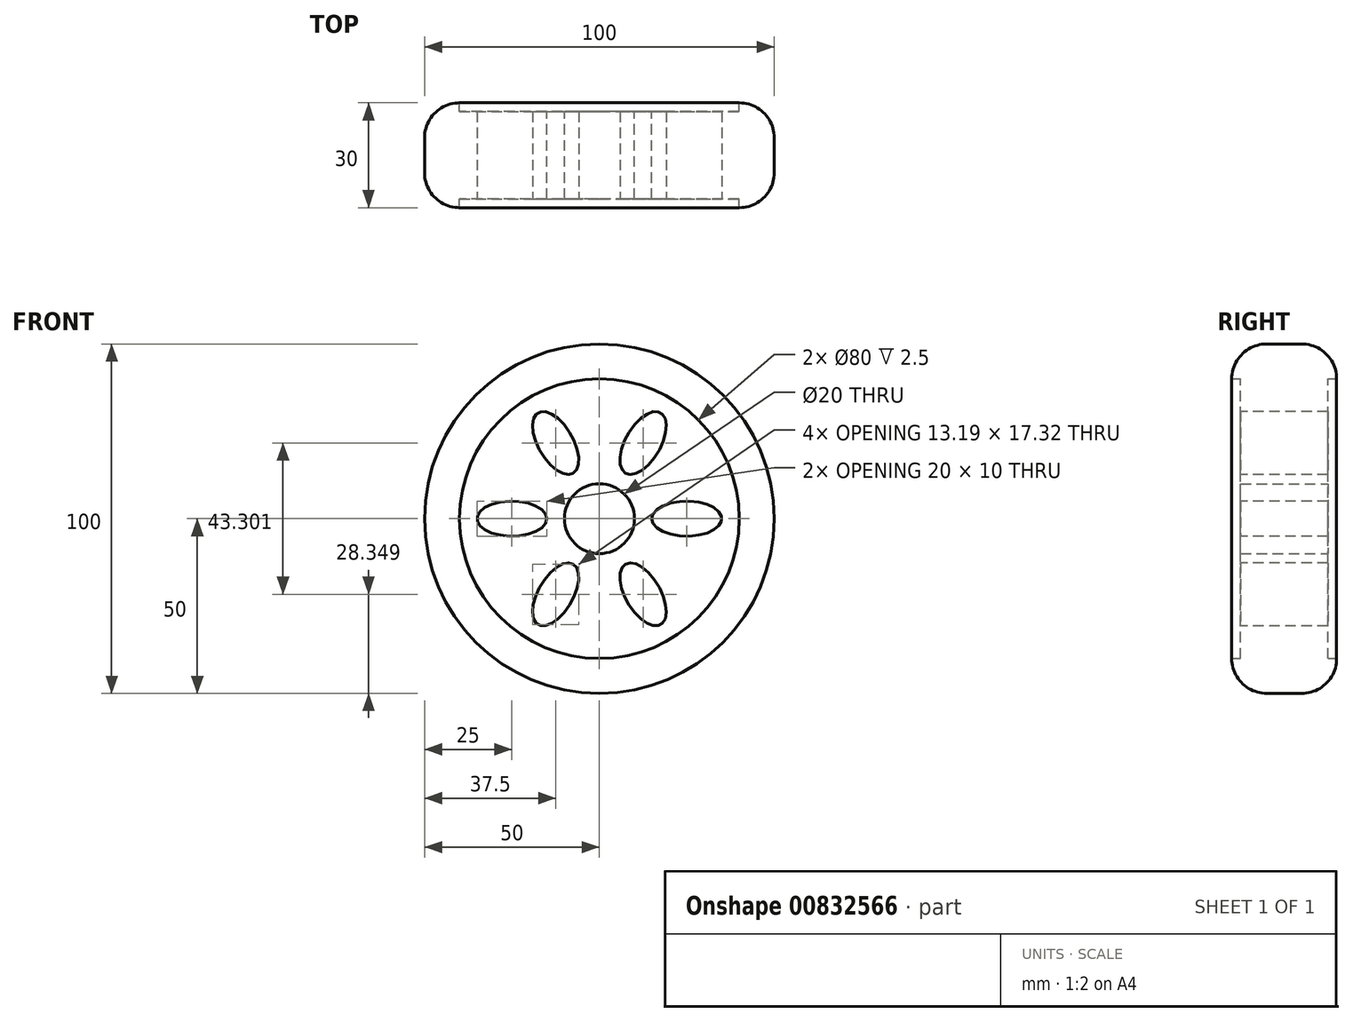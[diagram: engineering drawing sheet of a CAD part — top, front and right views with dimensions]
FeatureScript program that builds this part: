
annotation { "Feature Type Name" : "Feature", "Feature Type Description" : "" }
export const myFeature = defineFeature(function(context is Context, id is Id, definition is map)
    precondition{}
    {
        {
            var Q0;
            Q0=qCreatedBy(makeId("Front.planeOp"),FACE);
            var sketch = newSketch(context, id + "F0", { "sketchPlane" : qUnion([Q0])});
            skCircle(sketch, "E0", {"center": v(0, 0) * mm, "radius": 50 * mm});
            skCircle(sketch, "E1", {"center": v(0, 0) * mm, "radius": 40 * mm});
            skSolve(sketch);
        }
        {
            var Q0;
            Q0=makeQuery(id+"F0.imprint","IMPRINT",FACE,{"disambiguationData":[TD([[makeQuery(id+"F0.imprint","IMPRINT",EDGE,{"derivedFrom":sQuery(id+"F0.wireOp",EDGE,"E0")}),1.0]])]});
            extrude(context, id + "F1", {"entities" : qUnion([Q0]), "endBound" : BoundingType.SYMMETRIC, "depth" : 30 * mm, "offsetDistance" : 25 * mm});
        }
        {
            var Q0;
            Q0=makeQuery(id+"F0.imprint","IMPRINT",FACE,{"disambiguationData":[TD([[makeQuery(id+"F0.imprint","IMPRINT",EDGE,{"derivedFrom":sQuery(id+"F0.wireOp",EDGE,"E1")}),1.0]])]});
            extrude(context, id + "F2", {"entities" : qUnion([Q0]), "operationType" : NewBodyOperationType.ADD, "endBound" : BoundingType.SYMMETRIC, "depth" : 25 * mm, "offsetDistance" : 25 * mm});
        }
        {
            var Q0;
            Q0=makeQuery(id+"F2.opExtrude","CAP_FACE",FACE,{"disambiguationData":[OSD([sQuery(id+"F0.wireOp",EDGE,"E1")])],"isStart":true});
            var sketch = newSketch(context, id + "F3", { "sketchPlane" : qUnion([Q0])});
            skEllipse(sketch, "E2", {"center": v(25, 0) * mm, "majorRadius": 10 * mm, "minorRadius": 5 * mm, "majorAxis": v(-1, 0)});
            skEllipse(sketch, "E3.1.0", {"center": v(12.5, 21.65) * mm, "majorRadius": 10 * mm, "minorRadius": 5 * mm, "majorAxis": v(-0.5, -0.87)});
            skEllipse(sketch, "E3.2.0", {"center": v(-12.5, 21.65) * mm, "majorRadius": 10 * mm, "minorRadius": 5 * mm, "majorAxis": v(0.5, -0.87)});
            skEllipse(sketch, "E3.3.0", {"center": v(-25, 0) * mm, "majorRadius": 10 * mm, "minorRadius": 5 * mm, "majorAxis": v(1, 0)});
            skEllipse(sketch, "E3.4.0", {"center": v(-12.5, -21.65) * mm, "majorRadius": 10 * mm, "minorRadius": 5 * mm, "majorAxis": v(0.5, 0.87)});
            skEllipse(sketch, "E3.5.0", {"center": v(12.5, -21.65) * mm, "majorRadius": 10 * mm, "minorRadius": 5 * mm, "majorAxis": v(-0.5, 0.87)});
            skPoint(sketch, "E3.center", {"position": v(0, 0) * mm});
            skSolve(sketch);
        }
        {
            var Q0;
            Q0=makeQuery(id+"F3.imprint","IMPRINT",FACE,{"disambiguationData":[TD([[makeQuery(id+"F3.imprint","IMPRINT",EDGE,{"derivedFrom":sQuery(id+"F3.wireOp",EDGE,"E3.1.0")}),1.0]])]});
            var Q1;
            Q1=makeQuery(id+"F3.imprint","IMPRINT",FACE,{"disambiguationData":[TD([[makeQuery(id+"F3.imprint","IMPRINT",EDGE,{"derivedFrom":sQuery(id+"F3.wireOp",EDGE,"E2")}),1.0]])]});
            var Q2;
            Q2=makeQuery(id+"F3.imprint","IMPRINT",FACE,{"disambiguationData":[TD([[makeQuery(id+"F3.imprint","IMPRINT",EDGE,{"derivedFrom":sQuery(id+"F3.wireOp",EDGE,"E3.5.0")}),1.0]])]});
            var Q3;
            Q3=makeQuery(id+"F3.imprint","IMPRINT",FACE,{"disambiguationData":[TD([[makeQuery(id+"F3.imprint","IMPRINT",EDGE,{"derivedFrom":sQuery(id+"F3.wireOp",EDGE,"E3.4.0")}),1.0]])]});
            var Q4;
            Q4=makeQuery(id+"F3.imprint","IMPRINT",FACE,{"disambiguationData":[TD([[makeQuery(id+"F3.imprint","IMPRINT",EDGE,{"derivedFrom":sQuery(id+"F3.wireOp",EDGE,"E3.3.0")}),1.0]])]});
            var Q5;
            Q5=makeQuery(id+"F3.imprint","IMPRINT",FACE,{"disambiguationData":[TD([[makeQuery(id+"F3.imprint","IMPRINT",EDGE,{"derivedFrom":sQuery(id+"F3.wireOp",EDGE,"E3.2.0")}),1.0]])]});
            extrude(context, id + "F4", {"entities" : qUnion([Q0, Q1, Q2, Q3, Q4, Q5]), "operationType" : NewBodyOperationType.REMOVE, "endBound" : BoundingType.UP_TO_NEXT, "oppositeDirection" : true, "depth" : 25 * mm, "offsetDistance" : 25 * mm});
        }
        {
            var Q0;
            Q0=makeQuery(id+"F2.opExtrude","CAP_FACE",FACE,{"disambiguationData":[OSD([sQuery(id+"F0.wireOp",EDGE,"E1")])],"isStart":true});
            var sketch = newSketch(context, id + "F5", { "sketchPlane" : qUnion([Q0])});
            skCircle(sketch, "E4", {"center": v(0, 0) * mm, "radius": 10 * mm});
            skSolve(sketch);
        }
        {
            var Q0;
            Q0=makeQuery(id+"F5.imprint","IMPRINT",FACE,{"disambiguationData":[TD([[makeQuery(id+"F5.imprint","IMPRINT",EDGE,{"derivedFrom":sQuery(id+"F5.wireOp",EDGE,"E4")}),1.0]])]});
            extrude(context, id + "F6", {"entities" : qUnion([Q0]), "operationType" : NewBodyOperationType.REMOVE, "endBound" : BoundingType.UP_TO_NEXT, "oppositeDirection" : true, "depth" : 25 * mm, "offsetDistance" : 25 * mm});
        }
        {
            var Q0;
            Q0=makeQuery(id+"F1.opExtrude","CAP_EDGE",EDGE,{"disambiguationData":[OSD([sQuery(id+"F0.wireOp",EDGE,"E0")])],"isStart":true});
            var Q1;
            Q1=makeQuery(id+"F1.opExtrude","CAP_EDGE",EDGE,{"disambiguationData":[OSD([sQuery(id+"F0.wireOp",EDGE,"E0")])],"isStart":false});
            fillet(context, id + "F7", {"entities" : qUnion([Q0, Q1]), "radius" : 10 * mm, "tangentPropagation" : true, "allowEdgeOverflow" : false});
        }
    });
